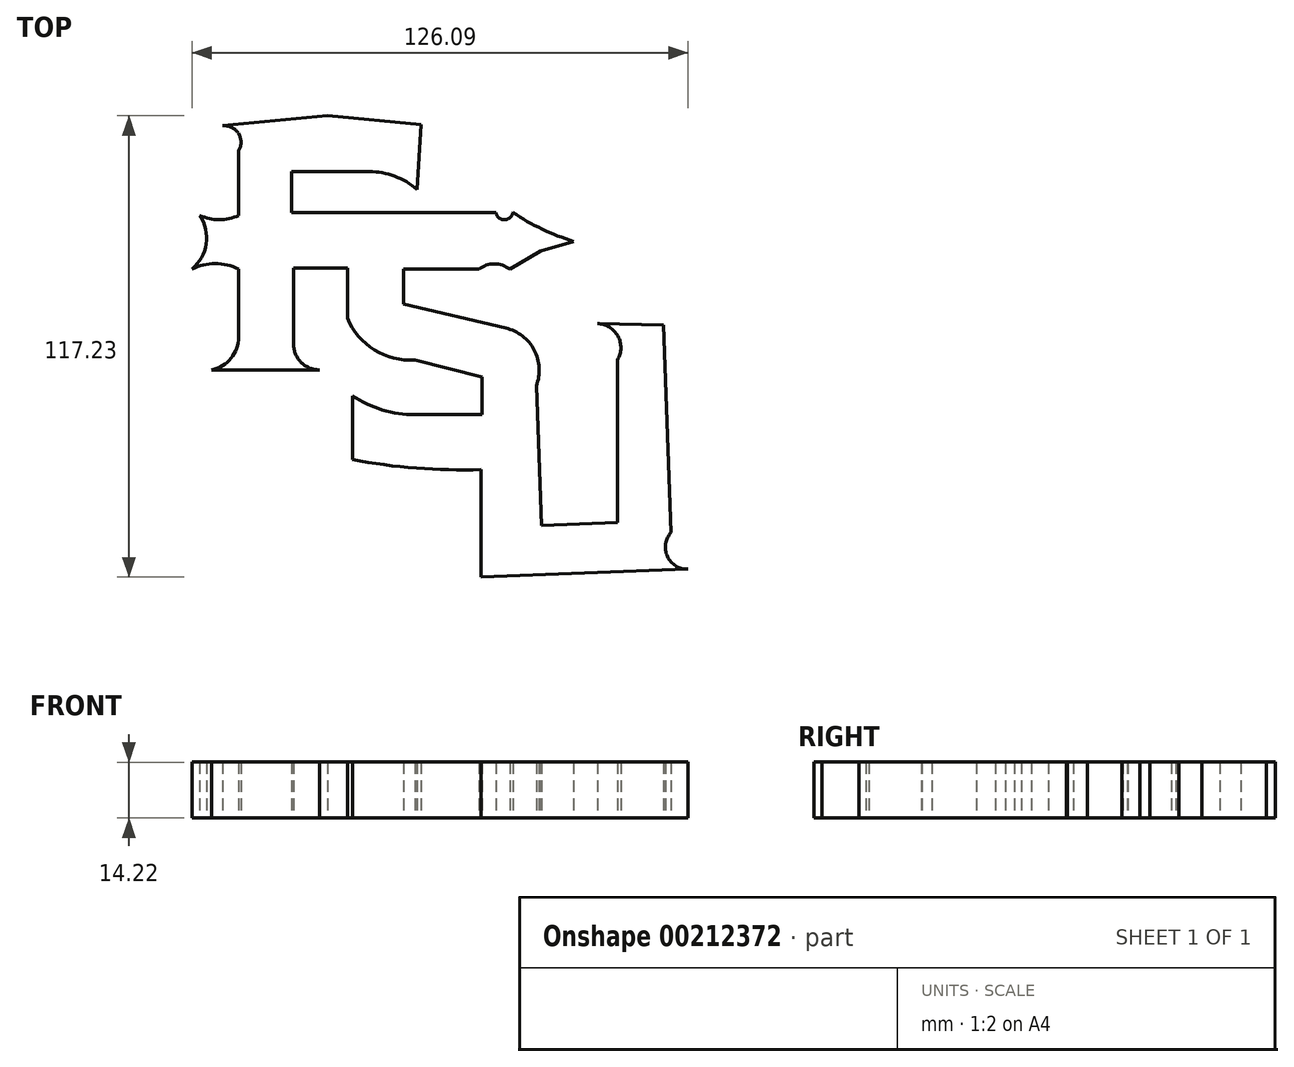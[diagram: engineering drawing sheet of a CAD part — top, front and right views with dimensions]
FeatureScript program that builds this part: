
annotation { "Feature Type Name" : "Feature", "Feature Type Description" : "" }
export const myFeature = defineFeature(function(context is Context, id is Id, definition is map)
    precondition{}
    {
        {
            var Q0;
            Q0=qCreatedBy(makeId("Top.planeOp"),FACE);
            var sketch = newSketch(context, id + "F0", { "sketchPlane" : qUnion([Q0])});
            skLineSegment(sketch, "E0", {"start": v(-9.12, 59.75) * mm, "end": v(-32.92, 62.03) * mm});
            skLineSegment(sketch, "E1", {"start": v(-32.92, 62.03) * mm, "end": v(-59.5, 59.5) * mm});
            skArc(sketch, "E2", {"start": v(-55.45, 53.17) * mm, "mid": v(-55.54, 57.57) * mm, "end": v(-59.5, 59.5) * mm});
            skLineSegment(sketch, "E3", {"start": v(-55.45, 53.17) * mm, "end": v(-55.45, 36.71) * mm});
            skArc(sketch, "E4", {"start": v(-65.32, 36.71) * mm, "mid": v(-60.39, 35.62) * mm, "end": v(-55.45, 36.71) * mm});
            skArc(sketch, "E5", {"start": v(-67.35, 23.04) * mm, "mid": v(-63.74, 29.5) * mm, "end": v(-65.32, 36.71) * mm});
            skArc(sketch, "E6", {"start": v(-55.45, 23.04) * mm, "mid": v(-61.4, 24.49) * mm, "end": v(-67.35, 23.04) * mm});
            skLineSegment(sketch, "E7", {"start": v(-55.45, 23.04) * mm, "end": v(-55.45, 5.82) * mm});
            skArc(sketch, "E8", {"start": v(-62.29, -2.53) * mm, "mid": v(-57.38, 0.43) * mm, "end": v(-55.45, 5.82) * mm});
            skLineSegment(sketch, "E9", {"start": v(-62.29, -2.53) * mm, "end": v(-34.94, -2.53) * mm});
            skArc(sketch, "E10", {"start": v(-41.52, 4.3) * mm, "mid": v(-39.69, -0.51) * mm, "end": v(-34.94, -2.53) * mm});
            skLineSegment(sketch, "E11", {"start": v(-41.52, 4.3) * mm, "end": v(-41.52, 23.3) * mm});
            skLineSegment(sketch, "E12", {"start": v(-41.52, 23.3) * mm, "end": v(-27.85, 23.3) * mm});
            skLineSegment(sketch, "E13", {"start": v(-27.85, 23.3) * mm, "end": v(-27.85, 10.63) * mm});
            skArc(sketch, "E14", {"start": v(-27.85, 10.63) * mm, "mid": v(-20.96, 2.53) * mm, "end": v(-10.63, 0) * mm});
            skLineSegment(sketch, "E15", {"start": v(-10.63, 0) * mm, "end": v(6.33, -4.3) * mm});
            skLineSegment(sketch, "E16", {"start": v(6.33, -4.3) * mm, "end": v(6.33, -13.93) * mm});
            skLineSegment(sketch, "E17", {"start": v(6.33, -13.93) * mm, "end": v(-10.63, -13.93) * mm});
            skArc(sketch, "E18", {"start": v(-26.59, -9.12) * mm, "mid": v(-18.96, -12.7) * mm, "end": v(-10.63, -13.93) * mm});
            skLineSegment(sketch, "E19", {"start": v(-26.59, -9.12) * mm, "end": v(-26.59, -25.32) * mm});
            skArc(sketch, "E20", {"start": v(-26.59, -25.32) * mm, "mid": v(-10.33, -27.5) * mm, "end": v(6.08, -27.85) * mm});
            skLineSegment(sketch, "E21", {"start": v(6.08, -27.85) * mm, "end": v(6.08, -55.2) * mm});
            skLineSegment(sketch, "E22", {"start": v(6.08, -55.2) * mm, "end": v(58.74, -53.17) * mm});
            skArc(sketch, "E23", {"start": v(54.44, -43.8) * mm, "mid": v(53.46, -49.93) * mm, "end": v(58.74, -53.17) * mm});
            skLineSegment(sketch, "E24", {"start": v(54.44, -43.8) * mm, "end": v(52.41, 8.86) * mm});
            skLineSegment(sketch, "E25", {"start": v(52.41, 8.86) * mm, "end": v(35.7, 9.2) * mm});
            skArc(sketch, "E26", {"start": v(40.76, 0) * mm, "mid": v(40.9, 6.06) * mm, "end": v(35.7, 9.2) * mm});
            skLineSegment(sketch, "E27", {"start": v(40.76, 0) * mm, "end": v(40.76, -41.27) * mm});
            skLineSegment(sketch, "E28", {"start": v(40.76, -41.27) * mm, "end": v(21.53, -42.01) * mm});
            skLineSegment(sketch, "E29", {"start": v(21.53, -42.01) * mm, "end": v(20.17, -6.58) * mm});
            skArc(sketch, "E30", {"start": v(20.17, -6.58) * mm, "mid": v(19.62, 2.53) * mm, "end": v(12.4, 8.1) * mm});
            skLineSegment(sketch, "E31", {"start": v(12.4, 8.1) * mm, "end": v(-13.56, 14.22) * mm});
            skLineSegment(sketch, "E32", {"start": v(-13.56, 14.22) * mm, "end": v(-13.56, 23.04) * mm});
            skLineSegment(sketch, "E33", {"start": v(-13.56, 23.04) * mm, "end": v(5.57, 23.04) * mm});
            skArc(sketch, "E34", {"start": v(13.42, 23.04) * mm, "mid": v(9.5, 24.41) * mm, "end": v(5.57, 23.04) * mm});
            skLineSegment(sketch, "E35", {"start": v(13.42, 23.04) * mm, "end": v(21.27, 27.6) * mm});
            skLineSegment(sketch, "E36", {"start": v(21.27, 27.6) * mm, "end": v(29.62, 30.13) * mm});
            skArc(sketch, "E37", {"start": v(14.18, 37.47) * mm, "mid": v(21.63, 33.22) * mm, "end": v(29.62, 30.13) * mm});
            skArc(sketch, "E38", {"start": v(9.87, 37.47) * mm, "mid": v(12.03, 35.6) * mm, "end": v(14.18, 37.47) * mm});
            skLineSegment(sketch, "E39", {"start": v(9.87, 37.47) * mm, "end": v(-42.03, 37.47) * mm});
            skLineSegment(sketch, "E40", {"start": v(-42.03, 37.47) * mm, "end": v(-42.03, 47.85) * mm});
            skLineSegment(sketch, "E41", {"start": v(-42.03, 47.85) * mm, "end": v(-22.28, 47.85) * mm});
            skArc(sketch, "E42", {"start": v(-10.13, 43.3) * mm, "mid": v(-15.8, 46.68) * mm, "end": v(-22.28, 47.85) * mm});
            skLineSegment(sketch, "E43", {"start": v(-9.12, 59.75) * mm, "end": v(-10.13, 43.3) * mm});
            skSolve(sketch);
        }
        {
            var Q0;
            Q0 = qSketchRegion(id + "F0", true);
            extrude(context, id + "F1", {"entities" : qUnion([Q0]), "depth" : 14.22 * mm});
        }
    });
